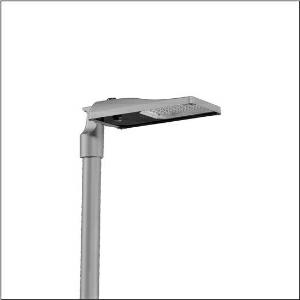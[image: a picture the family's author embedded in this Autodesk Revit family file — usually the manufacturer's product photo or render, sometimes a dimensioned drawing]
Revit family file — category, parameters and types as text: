
# Revit family: streetlight_sl_31_mini___stw1_0a_5xh6e31t08ja_04bd
name_source: partatom
category: Lighting Fixtures
units: mm (PartAtom-declared; Revit-internal decimal feet)

## family parameters
Cut with Voids When Loaded = No
Host = Face
Light Source = No
Part Type = Normal
Room Calculation Point = No
Round Connector Dimension = Use Diameter
Shared = No

## types (1)
- --- (1 x LED, 12270 lm, 82.5 W, 3000K)
    Apparent Load = 83 VA
    CIE Flux Codes = 39 75 98 100 100
    Color Rendering = 70
    Color Temperature = 3000K
    Default Elevation = 1800 mm
    Description = Streetlight SL 31 mini D4i, Desk-Remote mast luminaire for post-top, side-entry; light control with lens of PMMA; light distribution: STW1.0a, direct asymmetric distribution, for standard-compliant lighting for roads and squares; LED: luminous flux: 12.270lm, light colour: 730, colour temperature: 3000K; luminous efficacy: 148,7lm/W; control: pre-setting: logarithmic dimming characteristic, flexible luminous flux parameterisation, time-dependent luminous flux control, constant luminous flux control, power reduction, intelligent temperature release in ECG and LED module, overheat protection; luminaire housing, of diecast aluminium, Siteco® metallic grey (DB 702S), corrosivity category C5 high according to DIN EN ISO 12944; cover of toughened safety glass, transparent, opened without tools; mast flange of diecast aluminium, Siteco® metallic grey (DB 702S), spigot size: 76/60mm, mast flange included unmounted; with cable H07RN-F 2x 1.5mm², cable length: 10,5m, connection cable pre-assembled; mains connection: 220..240V, AC, 50/60Hz; power consumption (at start of service life): 82,5W / (at end of service life): 90,1W / (with reduced operation 50%): 36,8W; protection rating (complete): IP66; insulation class (complete): insulation class II (safety insulation); impact resistance: IK09; certification: CE, ENEC, ENEC+, VDE, UKCA, ZD4i; permissible operating ambient temperature for outdoor applications: -40..+50°C; packaging unit: 1 piece

Light Distribution: STW1.0a
    Height = 76 mm
    Lamp = 1 x LED
    Lamp Light Flux = 12270 lm
    Lamp Power = 82.5 W
    Lamp count = 1
    Length = 547 mm
    Luminous efficacy = 149 lm/W
    Manufacturer = Siteco
    ModVariant = No
    Model = 5XH6E31T08JA
    Number of Poles = 1
    OnlyDefault = Yes
    Power Factor = 1
    Product Name = Streetlight SL 31 mini | STW1.0a
    Product group = mast luminaire | pylon top
    ProductGroupID = 6100
    Protection Class = Protection class II
    Protection Degree = IP 66
    RLX_Detail_Level = 1
    RLX_Emergency_Light_Flux = 0 lm
    RLX_Emergency_Type = 0
    RLX_Emergency_Type_DB = No
    RlxData = <blob elided: 39989 chars, md5=fbfccb6f>
    Socket = socket
    Standby Power = 0 W
    System Light Flux = 12270 lm
    System Power = 83 W
    Type Comments = factory setting: luminous flux: 100 % | dim-lin: 254 | 870 mA
    Type Image = l_1300332.jpg
    URL = http://relux.com
    VarID = @adj_049846
    Voltage = 0 V
    Weight = 0.00 kg
    Width = 265 mm

## geometry (parser evidence)
native form markers: Blend x4, Sweep x10
no freeform markers — native parametric forms only
